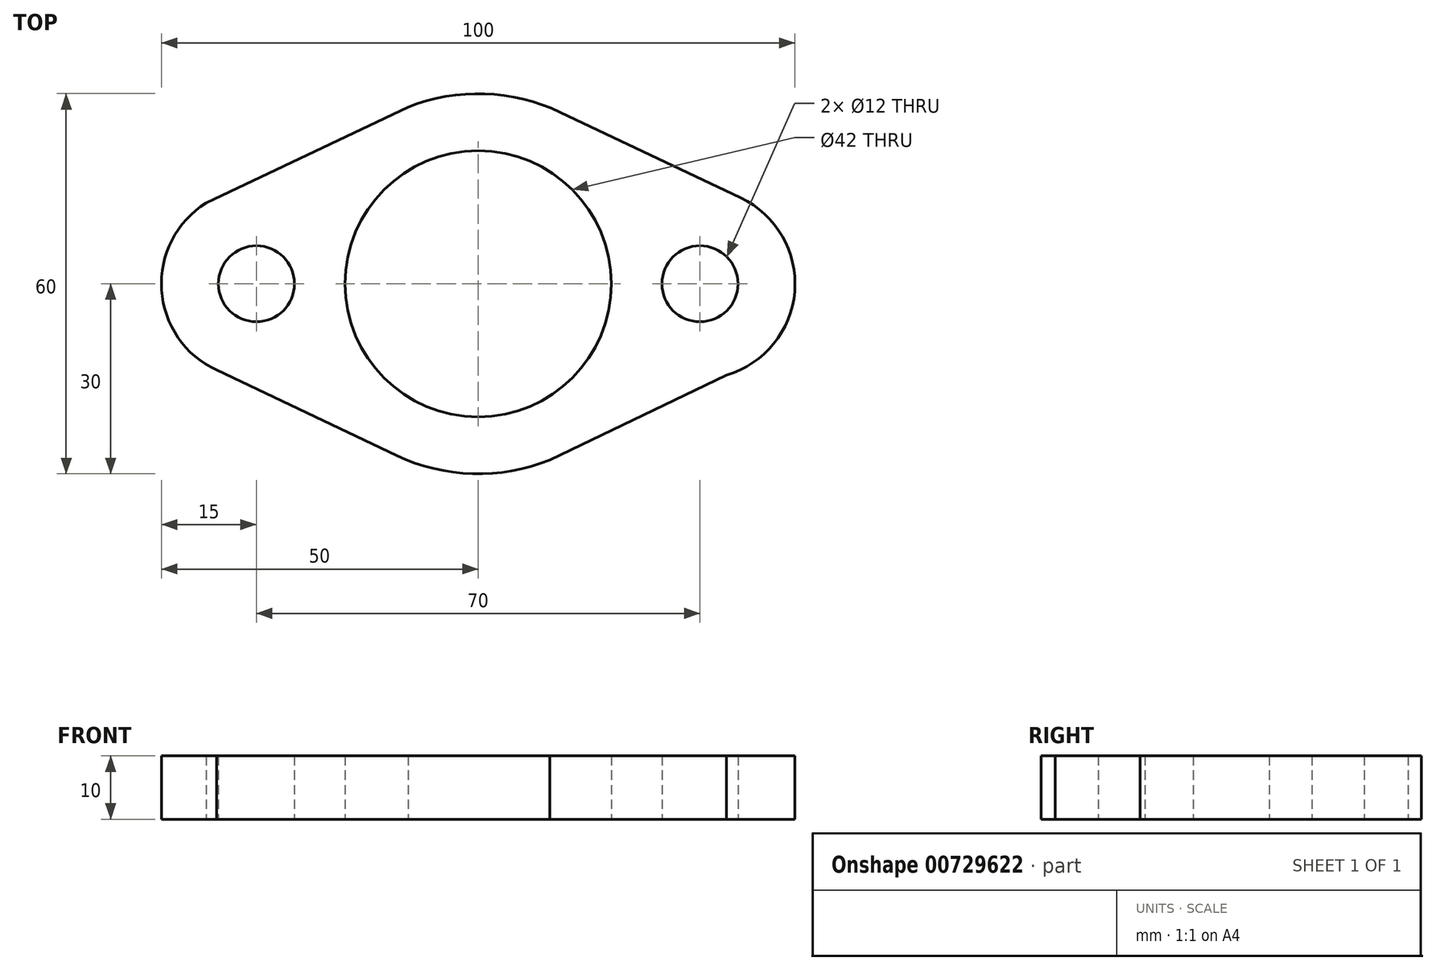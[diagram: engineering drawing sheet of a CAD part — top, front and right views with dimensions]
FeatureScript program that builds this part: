
annotation { "Feature Type Name" : "Feature", "Feature Type Description" : "" }
export const myFeature = defineFeature(function(context is Context, id is Id, definition is map)
    precondition{}
    {
        {
            var Q0;
            Q0=qCreatedBy(makeId("Top.planeOp"),FACE);
            var sketch = newSketch(context, id + "F0", { "sketchPlane" : qUnion([Q0])});
            skCircle(sketch, "E0", {"center": v(0, 0) * mm, "radius": 21 * mm});
            skArc(sketch, "E1", {"start": v(-12.86, -27.1) * mm, "mid": v(-0.86, -29.99) * mm, "end": v(11.29, -27.8) * mm});
            skArc(sketch, "E2", {"start": v(-42.94, 12.73) * mm, "mid": v(-49.97, -0.95) * mm, "end": v(-41.27, -13.63) * mm});
            skArc(sketch, "E3", {"start": v(39.2, -14.4) * mm, "mid": v(49.95, -1.2) * mm, "end": v(41.43, 13.55) * mm});
            skCircle(sketch, "E4", {"center": v(-35, 0) * mm, "radius": 6 * mm});
            skCircle(sketch, "E5", {"center": v(35, 0) * mm, "radius": 6 * mm});
            skLineSegment(sketch, "E6", {"start": v(-42.94, 12.73) * mm, "end": v(-11.05, 27.9) * mm});
            skLineSegment(sketch, "E7", {"start": v(12.8, 27.14) * mm, "end": v(41.43, 13.55) * mm});
            skLineSegment(sketch, "E8", {"start": v(-41.27, -13.63) * mm, "end": v(-12.86, -27.1) * mm});
            skLineSegment(sketch, "E9", {"start": v(11.29, -27.8) * mm, "end": v(39.2, -14.4) * mm});
            skArc(sketch, "E10.trimOffspring", {"start": v(12.92, 27.07) * mm, "mid": v(1.02, 29.98) * mm, "end": v(-11.05, 27.9) * mm});
            skSolve(sketch);
        }
        {
            var Q0;
            Q0 = qSketchRegion(id + "F0", true);
            extrude(context, id + "F1", {"entities" : qUnion([Q0]), "depth" : 10 * mm, "offsetDistance" : 25 * mm});
        }
    });
